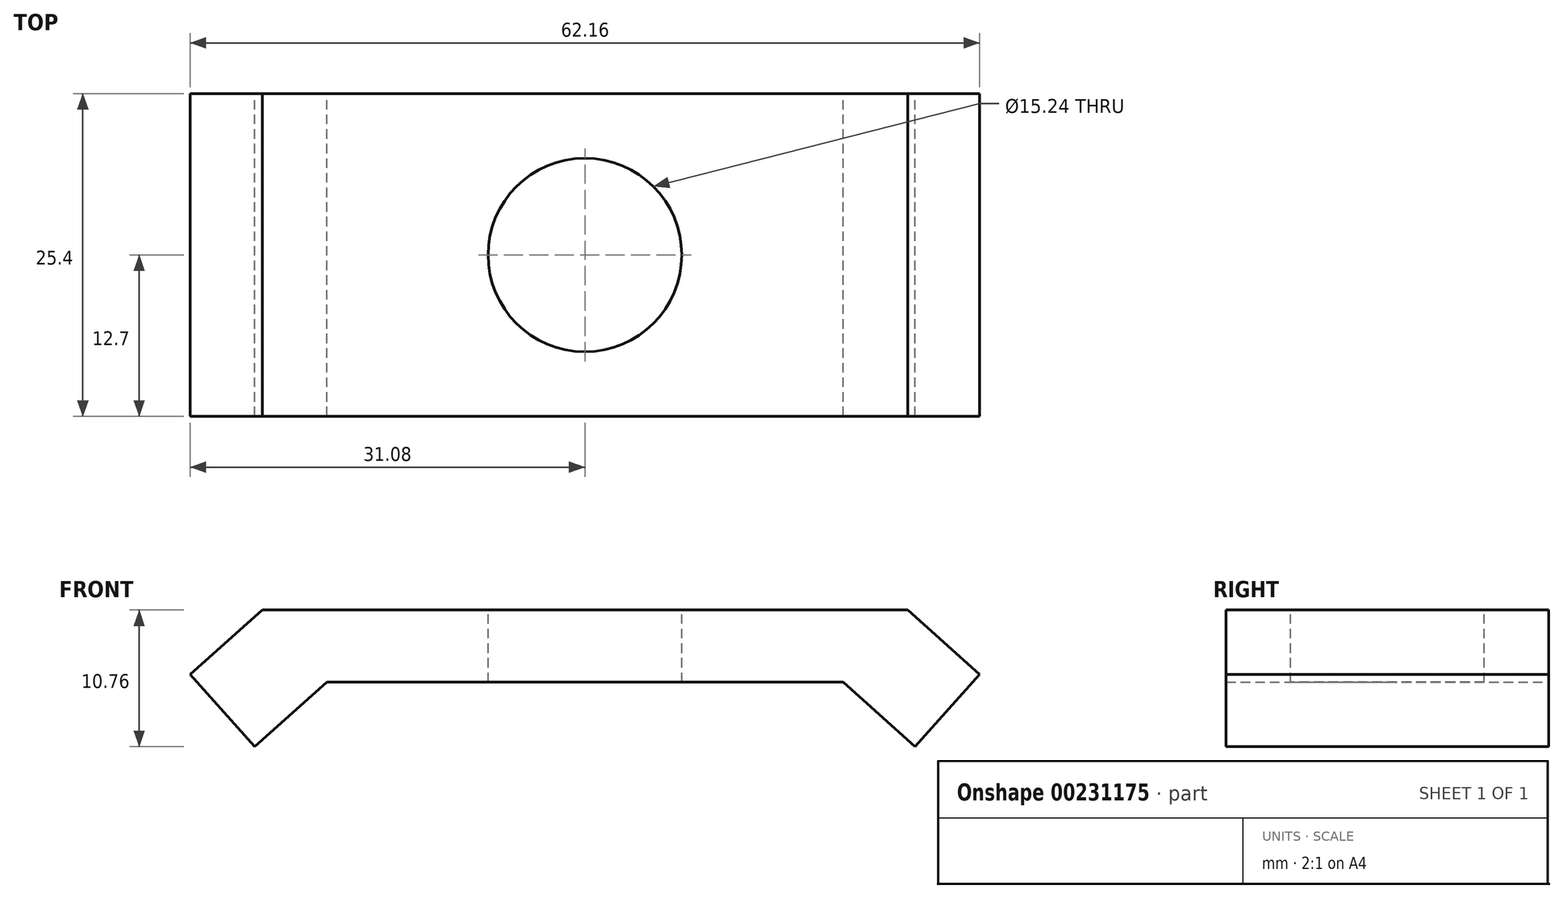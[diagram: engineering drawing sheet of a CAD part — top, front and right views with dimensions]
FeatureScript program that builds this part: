
annotation { "Feature Type Name" : "Feature", "Feature Type Description" : "" }
export const myFeature = defineFeature(function(context is Context, id is Id, definition is map)
    precondition{}
    {
        {
            var Q0;
            Q0=qCreatedBy(makeId("Front.planeOp"),FACE);
            var sketch = newSketch(context, id + "F0", { "sketchPlane" : qUnion([Q0])});
            skLineSegment(sketch, "E0", {"start": v(-26, 0) * mm, "end": v(-31.08, 5.68) * mm});
            skLineSegment(sketch, "E1", {"start": v(-31.08, 5.68) * mm, "end": v(-25.4, 10.76) * mm});
            skLineSegment(sketch, "E2", {"start": v(-25.4, 10.76) * mm, "end": v(0, 10.76) * mm});
            skLineSegment(sketch, "E3", {"start": v(-26, 0) * mm, "end": v(-20.32, 5.08) * mm});
            skLineSegment(sketch, "E4.MirrorCS", {"start": v(25.4, 10.76) * mm, "end": v(0, 10.76) * mm});
            skLineSegment(sketch, "E5.MirrorCS", {"start": v(26, 0) * mm, "end": v(20.32, 5.08) * mm});
            skLineSegment(sketch, "E6.MirrorCS", {"start": v(26, 0) * mm, "end": v(31.08, 5.68) * mm});
            skLineSegment(sketch, "E7.MirrorCS", {"start": v(31.08, 5.68) * mm, "end": v(25.4, 10.76) * mm});
            skLineSegment(sketch, "E8", {"start": v(-20.32, 5.08) * mm, "end": v(0, 5.08) * mm});
            skLineSegment(sketch, "E9", {"start": v(0, 5.08) * mm, "end": v(20.32, 5.08) * mm});
            skSolve(sketch);
        }
        {
            var Q0;
            Q0 = qSketchRegion(id + "F0", true);
            extrude(context, id + "F1", {"entities" : qUnion([Q0]), "depth" : 25.4 * mm});
        }
        {
            var Q0;
            Q0=makeQuery(id+"F1.opExtrude","SWEPT_FACE",FACE,{"disambiguationData":[OSD([sQuery(id+"F0.wireOp",EDGE,"E2"),sQuery(id+"F0.wireOp",EDGE,"E4.MirrorCS")])]});
            var sketch = newSketch(context, id + "F2", { "sketchPlane" : qUnion([Q0])});
            skCircle(sketch, "E10", {"center": v(0, -12.7) * mm, "radius": 7.62 * mm});
            skSolve(sketch);
        }
        {
            var Q0;
            Q0=sQuery(id+"F2.wireOp",VERTEX,"E10.center");
            var Q1;
            Q1=makeQuery(id+"F1.opExtrude","SWEPT_BODY",BODY,{"disambiguationData":[OSD([sQuery(id+"F0.wireOp",EDGE,"E0"),sQuery(id+"F0.wireOp",EDGE,"E1"),sQuery(id+"F0.wireOp",EDGE,"E2"),sQuery(id+"F0.wireOp",EDGE,"E3"),sQuery(id+"F0.wireOp",EDGE,"E2"),sQuery(id+"F0.wireOp",EDGE,"E4.MirrorCS"),sQuery(id+"F0.wireOp",EDGE,"E4.MirrorCS"),sQuery(id+"F0.wireOp",EDGE,"E5.MirrorCS"),sQuery(id+"F0.wireOp",EDGE,"E6.MirrorCS"),sQuery(id+"F0.wireOp",EDGE,"E7.MirrorCS")])]});
            hole(context, id + "F3", {"style" : HoleStyle.SIMPLE, "endStyle" : HoleEndStyle.THROUGH, "holeDiameter" : 15.24 * mm, "locations" : qUnion([Q0]), "scope" : qUnion([Q1]), "isTappedThrough" : true});
        }
    });
